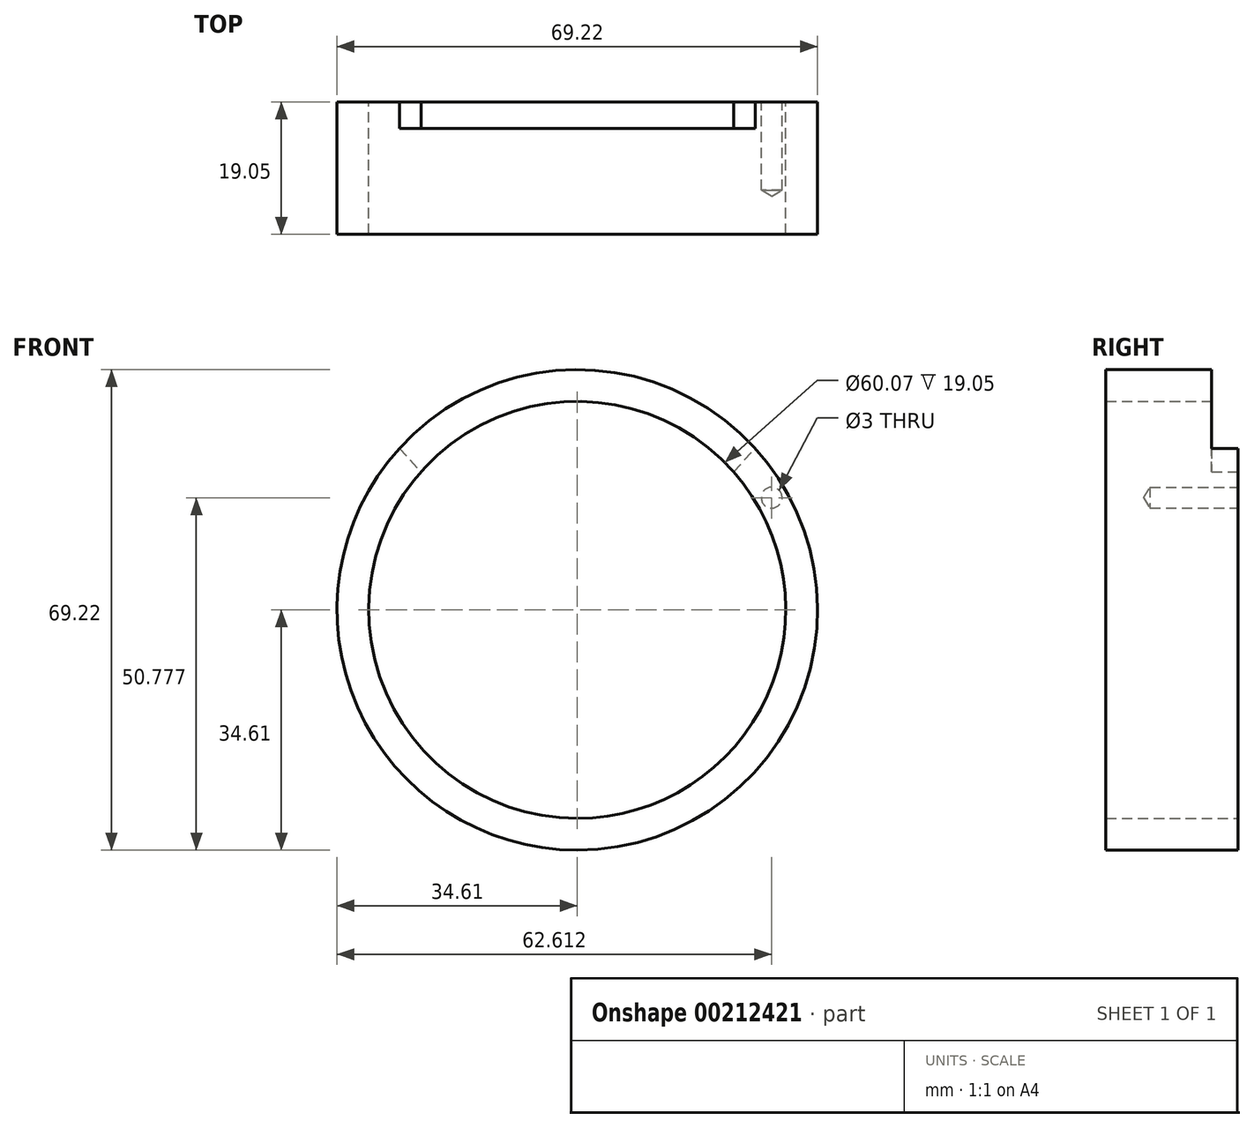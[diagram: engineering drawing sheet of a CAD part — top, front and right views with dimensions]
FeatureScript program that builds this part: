
annotation { "Feature Type Name" : "Feature", "Feature Type Description" : "" }
export const myFeature = defineFeature(function(context is Context, id is Id, definition is map)
    precondition{}
    {
        {
            var Q0;
            Q0=qCreatedBy(makeId("Front.planeOp"),FACE);
            var sketch = newSketch(context, id + "F0", { "sketchPlane" : qUnion([Q0])});
            skCircle(sketch, "E0", {"center": v(0, 0) * mm, "radius": 30.04 * mm});
            skCircle(sketch, "E1", {"center": v(0, 0) * mm, "radius": 34.6 * mm});
            skSolve(sketch);
        }
        {
            var Q0;
            Q0=qCreatedBy(makeId("Front.planeOp"),FACE);
            var sketch = newSketch(context, id + "F1", { "sketchPlane" : qUnion([Q0])});
            skLineSegment(sketch, "E2", {"start": v(0, 0) * mm, "end": v(0, 38.1) * mm, "construction": true});
            skLineSegment(sketch, "E3", {"start": v(0, 0) * mm, "end": v(-25.74, 28.1) * mm, "construction": true});
            skLineSegment(sketch, "E4", {"start": v(0, 0) * mm, "end": v(25.74, 28.1) * mm, "construction": true});
            skArc(sketch, "E5", {"start": v(25.74, 28.1) * mm, "mid": v(0, 38.1) * mm, "end": v(-25.74, 28.1) * mm});
            skLineSegment(sketch, "E6", {"start": v(-25.74, 28.1) * mm, "end": v(-28.08, 25.95) * mm});
            skLineSegment(sketch, "E7", {"start": v(-28.08, 25.95) * mm, "end": v(0, -4.7) * mm});
            skLineSegment(sketch, "E8", {"start": v(0, -4.7) * mm, "end": v(28.08, 25.95) * mm});
            skLineSegment(sketch, "E9", {"start": v(28.08, 25.95) * mm, "end": v(25.74, 28.1) * mm});
            skSolve(sketch);
        }
        {
            var Q0;
            Q0 = qSketchRegion(id + "F0", true);
            extrude(context, id + "F2", {"entities" : qUnion([Q0]), "depth" : 19.05 * mm});
        }
        {
            var Q0;
            Q0 = qSketchRegion(id + "F1", true);
            extrude(context, id + "F3", {"entities" : qUnion([Q0]), "operationType" : NewBodyOperationType.REMOVE, "depth" : 3.8 * mm});
        }
        {
            var Q0;
            Q0=qCreatedBy(makeId("Front.planeOp"),FACE);
            var sketch = newSketch(context, id + "F4", { "sketchPlane" : qUnion([Q0])});
            skLineSegment(sketch, "E10", {"start": v(0, 0) * mm, "end": v(26.48, 18.54) * mm, "construction": true});
            skLineSegment(sketch, "E11", {"start": v(0, 0) * mm, "end": v(28, 16.17) * mm});
            skLineSegment(sketch, "E12", {"start": v(0, 0) * mm, "end": v(0, 32.33) * mm});
            skSolve(sketch);
        }
        {
            var Q0;
            Q0=sQuery(id+"F4.wireOp",VERTEX,"E11.end");
            var Q1;
            Q1=makeQuery(id+"F2.opExtrude","SWEPT_BODY",BODY,{"disambiguationData":[OSD([sQuery(id+"F0.wireOp",EDGE,"E0"),sQuery(id+"F0.wireOp",EDGE,"E1")])]});
            hole(context, id + "F5", {"style" : HoleStyle.SIMPLE, "endStyle" : HoleEndStyle.BLIND, "oppositeDirection" : true, "holeDiameter" : 3 * mm, "holeDepth" : 12.7 * mm, "locations" : qUnion([Q0]), "scope" : qUnion([Q1])});
        }
    });
